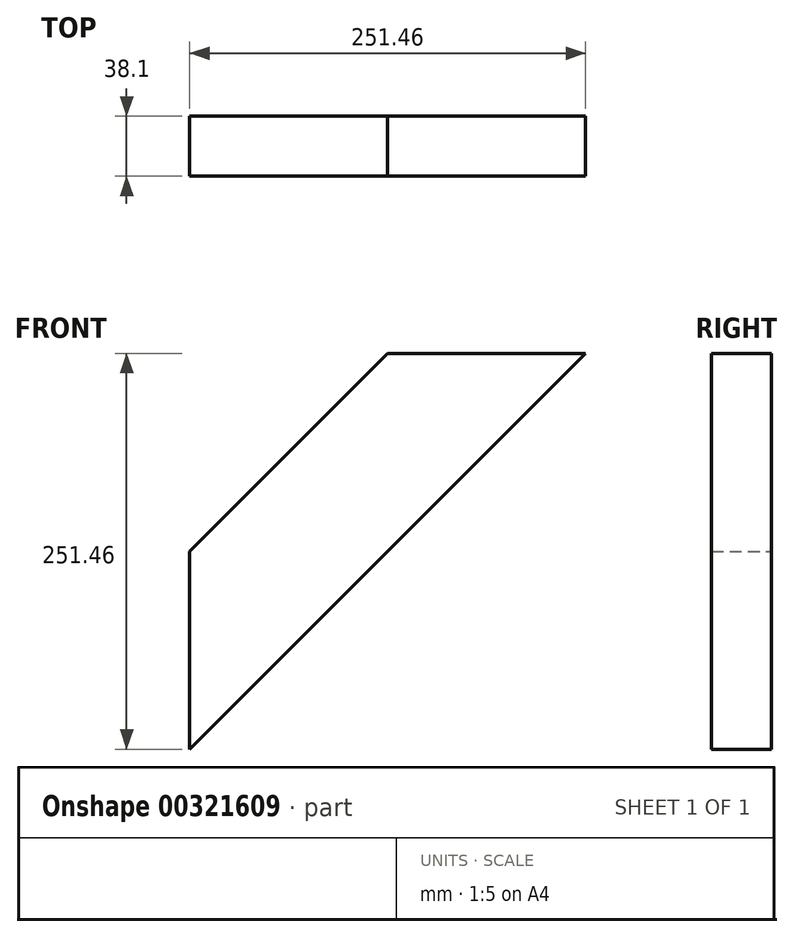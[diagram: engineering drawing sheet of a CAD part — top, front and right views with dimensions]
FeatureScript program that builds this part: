
annotation { "Feature Type Name" : "Feature", "Feature Type Description" : "" }
export const myFeature = defineFeature(function(context is Context, id is Id, definition is map)
    precondition{}
    {
        {
            var Q0;
            Q0=qCreatedBy(makeId("Front.planeOp"),FACE);
            var sketch = newSketch(context, id + "F0", { "sketchPlane" : qUnion([Q0])});
            skLineSegment(sketch, "E0", {"start": v(-23, 99.47) * mm, "end": v(102.72, 99.47) * mm});
            skLineSegment(sketch, "E1", {"start": v(102.72, 99.47) * mm, "end": v(-148.74, -151.99) * mm});
            skLineSegment(sketch, "E2", {"start": v(-148.74, -151.99) * mm, "end": v(-148.74, -26.26) * mm});
            skLineSegment(sketch, "E3", {"start": v(-148.74, -26.26) * mm, "end": v(-23, 99.47) * mm});
            skSolve(sketch);
        }
        {
            var Q0;
            Q0=makeQuery(id+"F0.imprint","IMPRINT",FACE,{"disambiguationData":[TD([[makeQuery(id+"F0.imprint","IMPRINT",EDGE,{"derivedFrom":sQuery(id+"F0.wireOp",EDGE,"E0")}),-1.0]])]});
            extrude(context, id + "F1", {"entities" : qUnion([Q0]), "depth" : 38.1 * mm});
        }
    });
